# Revit family: UnoFloor Metering Comfort(Control)_RFA_1
name_source: partatom
category: Pipe Accessories
units: mm (PartAtom-declared; Revit-internal decimal feet)

## family parameters
Always vertical = Yes
Cut with Voids When Loaded = No
OmniClass Number = 23.65.55.14.17
OmniClass Title = Adjusting/Controlling Valves for Liquid Services
Part Type = Valve - Breaks Into
Round Connector Dimension = Use Diameter
Shared = No
Work Plane-Based = Yes

## types (4) — shared parameters
Body Material = Danfoss Steel (Zinc Plated and Painted White)
D = 20 mm  [stored 0.0656168 ft]
Default Elevation = 1219.2 mm  [stored 4 ft]
Description = Distribution Units
Flow 2 (DHW) = 0.0 m³/h
H = 939 mm  [stored 3.08071 ft]
H1 = 288.9 mm  [stored 0.947835 ft]
H2 = 110.6 mm  [stored 0.362861 ft]
IfcExportAs = IfcValveType
L1 = 50 mm  [stored 0.164042 ft]
LookupTableName = Unofloor Metering Comfort(Control)_Lookup
Manufacturer = Danfoss
Max Differential Pressure = 0.6 bar
Max Medium Temperature = 60 °C
Nominal Pressure = PN 6
Power = 0 VA
URL = https://store.danfoss.com
Voltage = 230 V
W = 111 mm

## per-type parameters (varying)
| type | IfcExportType | Left Assembly | Model | Pack Contents | Right Assembly | Type number |
| UnoFloor Metering Control_4L-12L | Unofloor Metering Control Left | Yes | 088X4224,088X4225,088X4226,088X4227,088X4228,088X4230,088X4232 | Danfoss Icon2™ Master controller 230V, Actuators, Stainless steel manifold, Spacer Heat meter, AB-PM, MTCV Balancing Valve | No | 3 |
| UnoFloor Metering Control_4R-12R | Unofloor Metering Control Right | No | 088X4234,088X4235,088X4236,088X4237,088X4238,088X4240,088X4242 | Danfoss Icon2™ Master controller 230V, Actuators, Stainless steel manifold, Spacer Heat meter, AB-PM, MTCV Balancing Valve | Yes | 4 |
| UnoFloor Metering Comfort_4L-12L | Unofloor Metering Comfort Left | Yes | 088X4104,088X4105,088X4106,088X4107,088X4108,088X4110,088X4112 | Danfoss Icon™ Wiring center 230V, Actuators, Stainless steel manifold, Spacer Heat meter, AB-PM, MTCV Balancing Valve | No | 1 |
| UnoFloor Metering Comfort_4R-12R | Unofloor Metering Comfort Right | No | 088X4114,088X4115,088X4116,088X4117,088X4118,088X4120,088X4122 | Danfoss Icon™ Wiring center 230V, Actuators, Stainless steel manifold, Spacer Heat meter, AB-PM, MTCV Balancing Valve | Yes | 2 |

note: [stored X ft] marks values corroborated as IEEE doubles in the binary element streams (Revit-internal decimal feet)

## geometry (parser evidence)
native form markers: Sweep x1
no freeform markers — native parametric forms only
